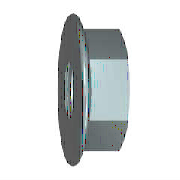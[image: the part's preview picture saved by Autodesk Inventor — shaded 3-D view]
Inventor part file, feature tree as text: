
AUTODESK INVENTOR PART (.ipt)
format: ipt  version: 2024 (Build 280153000, 153)  size: 200,704 bytes
history: native  units: mm (DEFAULTED — no unit token found)
features: other x3, extrude x1, hole x1, plane x1
ambient origin geometry x7: Origin, YZ Plane, XZ Plane, X Axis, Y Axis, Z Axis, Center Point
bodies: Solid1 (feature_tree)
feature tree (6):
  other  "Кольцо"
  extrude  "Базовый элемент"  Depth=42.8mm
  other  "Фаска1"
  hole  "Резьба"  [1 undecoded]
  other  "Work Axis1"
  plane  "Work Plane1"
note: 1 required parameter value undecoded (feature->parameter linkage not recoverable at this tier; creation-order binding heuristic only, values carry confidence <= 0.55)
